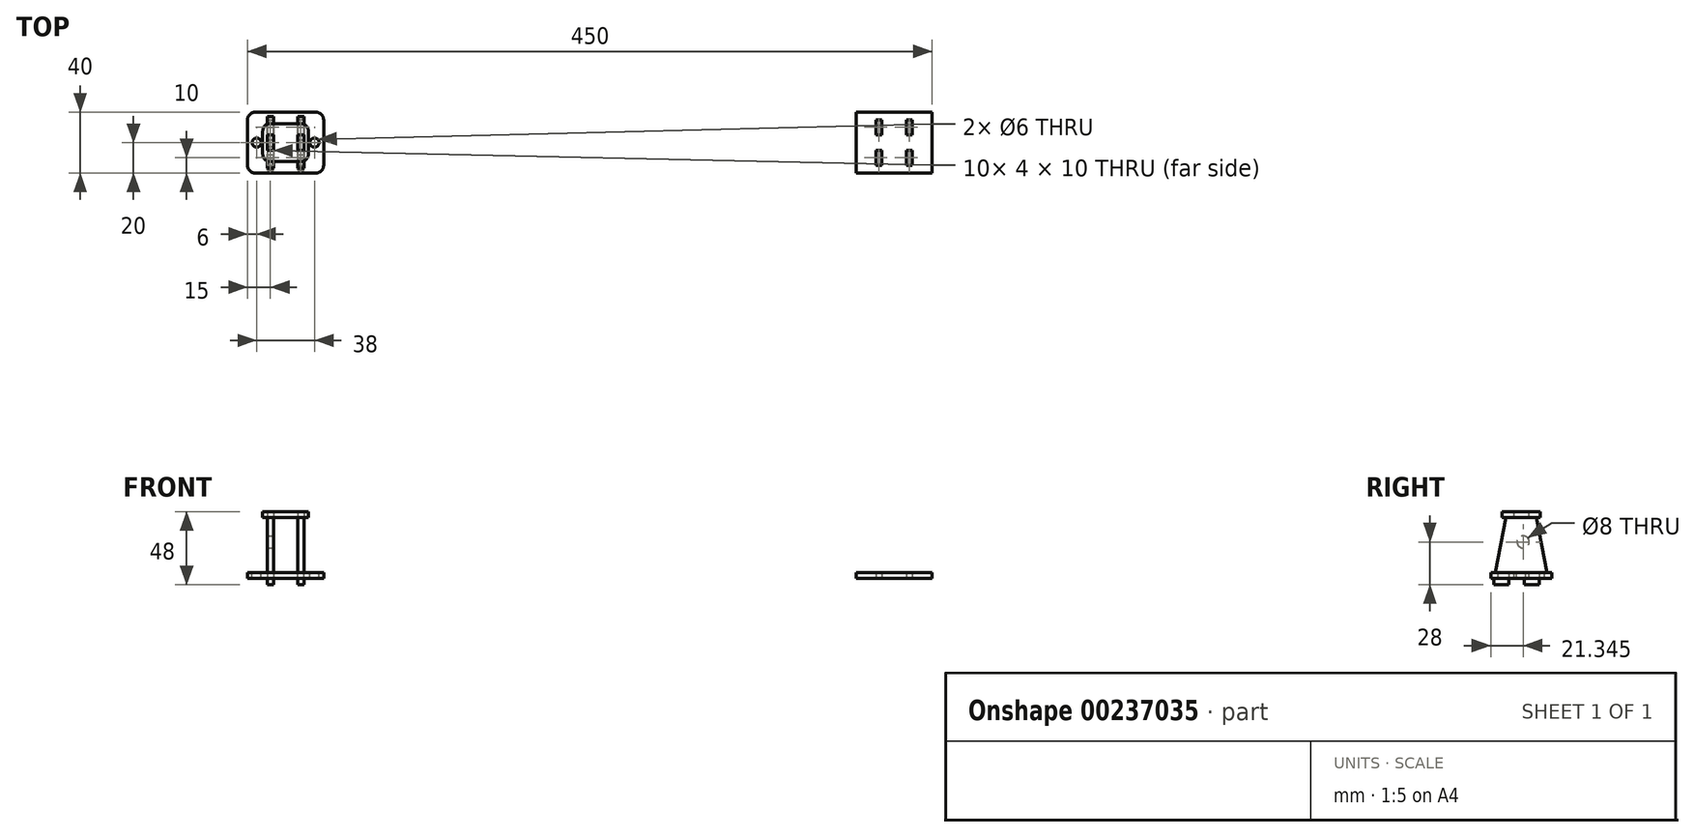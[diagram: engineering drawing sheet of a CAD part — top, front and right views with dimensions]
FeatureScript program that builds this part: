
annotation { "Feature Type Name" : "Feature", "Feature Type Description" : "" }
export const myFeature = defineFeature(function(context is Context, id is Id, definition is map)
    precondition{}
    {
        {
            var Q0;
            Q0=qCreatedBy(makeId("Top.planeOp"),FACE);
            var sketch = newSketch(context, id + "F0", { "sketchPlane" : qUnion([Q0])});
            skLineSegment(sketch, "E0.bottom", {"start": v(-200, 7.5) * mm, "end": v(200, 7.5) * mm});
            skLineSegment(sketch, "E0.top", {"start": v(-200, -7.5) * mm, "end": v(200, -7.5) * mm});
            skLineSegment(sketch, "E0.left", {"start": v(-200, 7.5) * mm, "end": v(-200, -7.5) * mm});
            skLineSegment(sketch, "E0.right", {"start": v(200, 7.5) * mm, "end": v(200, -7.5) * mm});
            skPoint(sketch, "E0.middle", {"position": v(0, 0) * mm});
            skSolve(sketch);
        }
        {
            var Q0;
            Q0=qCreatedBy(makeId("Top.planeOp"),FACE);
            var sketch = newSketch(context, id + "F1", { "sketchPlane" : qUnion([Q0])});
            skLineSegment(sketch, "E1.bottom", {"start": v(-225, 20) * mm, "end": v(-175, 20) * mm});
            skLineSegment(sketch, "E1.top", {"start": v(-225, -20) * mm, "end": v(-175, -20) * mm});
            skLineSegment(sketch, "E1.left", {"start": v(-225, 20) * mm, "end": v(-225, -20) * mm});
            skLineSegment(sketch, "E1.right", {"start": v(-175, 20) * mm, "end": v(-175, -20) * mm});
            skPoint(sketch, "E1.middle", {"position": v(-200, 0) * mm});
            skLineSegment(sketch, "E2.bottom", {"start": v(-212, 15) * mm, "end": v(-208, 15) * mm});
            skLineSegment(sketch, "E2.top", {"start": v(-212, 5) * mm, "end": v(-208, 5) * mm});
            skLineSegment(sketch, "E2.left", {"start": v(-212, 15) * mm, "end": v(-212, 5) * mm});
            skLineSegment(sketch, "E2.right", {"start": v(-208, 15) * mm, "end": v(-208, 5) * mm});
            skPoint(sketch, "E2.middle", {"position": v(-210, 10) * mm});
            skPoint(sketch, "E3.MirrorP", {"position": v(-210, -10) * mm});
            skLineSegment(sketch, "E4.MirrorCS", {"start": v(-212, -15) * mm, "end": v(-208, -15) * mm});
            skLineSegment(sketch, "E5.MirrorCS", {"start": v(-212, -15) * mm, "end": v(-212, -5) * mm});
            skLineSegment(sketch, "E6.MirrorCS", {"start": v(-208, -15) * mm, "end": v(-208, -5) * mm});
            skLineSegment(sketch, "E7.MirrorCS", {"start": v(-212, -5) * mm, "end": v(-208, -5) * mm});
            skLineSegment(sketch, "E8.MirrorCS", {"start": v(-188, -15) * mm, "end": v(-192, -15) * mm});
            skLineSegment(sketch, "E9.MirrorCS", {"start": v(-192, 15) * mm, "end": v(-192, 5) * mm});
            skLineSegment(sketch, "E10.MirrorCS", {"start": v(-188, 15) * mm, "end": v(-188, 5) * mm});
            skLineSegment(sketch, "E11.MirrorCS", {"start": v(-188, 5) * mm, "end": v(-192, 5) * mm});
            skLineSegment(sketch, "E12.MirrorCS", {"start": v(-188, 15) * mm, "end": v(-192, 15) * mm});
            skLineSegment(sketch, "E13.MirrorCS", {"start": v(-188, -15) * mm, "end": v(-188, -5) * mm});
            skLineSegment(sketch, "E14.MirrorCS", {"start": v(-188, -5) * mm, "end": v(-192, -5) * mm});
            skPoint(sketch, "E15.MirrorP", {"position": v(-190, 10) * mm});
            skPoint(sketch, "E16.MirrorP", {"position": v(-190, -10) * mm});
            skLineSegment(sketch, "E17.MirrorCS", {"start": v(-192, -15) * mm, "end": v(-192, -5) * mm});
            skLineSegment(sketch, "E18.MirrorCS", {"start": v(212, -15) * mm, "end": v(208, -15) * mm});
            skLineSegment(sketch, "E19.MirrorCS", {"start": v(188, -15) * mm, "end": v(192, -15) * mm});
            skLineSegment(sketch, "E20.MirrorCS", {"start": v(212, 15) * mm, "end": v(208, 15) * mm});
            skLineSegment(sketch, "E21.MirrorCS", {"start": v(212, -5) * mm, "end": v(208, -5) * mm});
            skLineSegment(sketch, "E22.MirrorCS", {"start": v(208, -15) * mm, "end": v(208, -5) * mm});
            skLineSegment(sketch, "E23.MirrorCS", {"start": v(212, -15) * mm, "end": v(212, -5) * mm});
            skLineSegment(sketch, "E24.MirrorCS", {"start": v(212, 5) * mm, "end": v(208, 5) * mm});
            skLineSegment(sketch, "E25.MirrorCS", {"start": v(188, 15) * mm, "end": v(192, 15) * mm});
            skLineSegment(sketch, "E26.MirrorCS", {"start": v(188, -15) * mm, "end": v(188, -5) * mm});
            skLineSegment(sketch, "E27.MirrorCS", {"start": v(192, -15) * mm, "end": v(192, -5) * mm});
            skLineSegment(sketch, "E28.MirrorCS", {"start": v(188, -5) * mm, "end": v(192, -5) * mm});
            skLineSegment(sketch, "E29.MirrorCS", {"start": v(188, 5) * mm, "end": v(192, 5) * mm});
            skLineSegment(sketch, "E30.MirrorCS", {"start": v(212, 15) * mm, "end": v(212, 5) * mm});
            skLineSegment(sketch, "E31.MirrorCS", {"start": v(188, 15) * mm, "end": v(188, 5) * mm});
            skLineSegment(sketch, "E32.MirrorCS", {"start": v(192, 15) * mm, "end": v(192, 5) * mm});
            skLineSegment(sketch, "E33.MirrorCS", {"start": v(208, 15) * mm, "end": v(208, 5) * mm});
            skLineSegment(sketch, "E34.MirrorCS", {"start": v(175, 20) * mm, "end": v(175, -20) * mm});
            skLineSegment(sketch, "E35.MirrorCS", {"start": v(225, 20) * mm, "end": v(225, -20) * mm});
            skLineSegment(sketch, "E36.MirrorCS", {"start": v(225, -20) * mm, "end": v(175, -20) * mm});
            skLineSegment(sketch, "E37.MirrorCS", {"start": v(225, 20) * mm, "end": v(175, 20) * mm});
            skPoint(sketch, "E38.MirrorP", {"position": v(210, 10) * mm});
            skPoint(sketch, "E39.MirrorP", {"position": v(190, 10) * mm});
            skPoint(sketch, "E40.MirrorP", {"position": v(200, 0) * mm});
            skPoint(sketch, "E41.MirrorP", {"position": v(190, -10) * mm});
            skPoint(sketch, "E42.MirrorP", {"position": v(210, -10) * mm});
            skSolve(sketch);
        }
        {
            var Q0;
            Q0 = qSketchRegion(id + "F1", true);
            extrude(context, id + "F2", {"entities" : qUnion([Q0]), "depth" : 4 * mm});
        }
        {
            var Q0;
            Q0=makeQuery(id+"F2.opExtrude","SWEPT_EDGE",EDGE,{"disambiguationData":[OSD([sQuery(id+"F1.wireOp",EDGE,"E1.bottom"),sQuery(id+"F1.wireOp",EDGE,"E1.right")])]});
            var Q1;
            Q1=makeQuery(id+"F2.opExtrude","SWEPT_EDGE",EDGE,{"disambiguationData":[OSD([sQuery(id+"F1.wireOp",EDGE,"E1.bottom"),sQuery(id+"F1.wireOp",EDGE,"E1.left")])]});
            var Q2;
            Q2=makeQuery(id+"F2.opExtrude","SWEPT_EDGE",EDGE,{"disambiguationData":[OSD([sQuery(id+"F1.wireOp",EDGE,"E1.top"),sQuery(id+"F1.wireOp",EDGE,"E1.right")])]});
            var Q3;
            Q3=makeQuery(id+"F2.opExtrude","SWEPT_EDGE",EDGE,{"disambiguationData":[OSD([sQuery(id+"F1.wireOp",EDGE,"E1.top"),sQuery(id+"F1.wireOp",EDGE,"E1.left")])]});
            fillet(context, id + "F3", {"entities" : qUnion([Q0, Q1, Q2, Q3]), "radius" : 5 * mm, "tangentPropagation" : true, "allowEdgeOverflow" : false});
        }
        {
            var Q0;
            Q0=makeQuery(id+"F2.opExtrude","SWEPT_FACE",FACE,{"disambiguationData":[OSD([sQuery(id+"F1.wireOp",EDGE,"E2.right")])]});
            var sketch = newSketch(context, id + "F4", { "sketchPlane" : qUnion([Q0])});
            skPoint(sketch, "E43.orphan", {"position": v(-10, 4) * mm});
            skLineSegment(sketch, "E44", {"start": v(-5, 44) * mm, "end": v(5, 44) * mm});
            skLineSegment(sketch, "E45", {"start": v(-5, 4) * mm, "end": v(-15, 4) * mm});
            skLineSegment(sketch, "E46", {"start": v(-10.11, 40) * mm, "end": v(-17, 4) * mm});
            skLineSegment(sketch, "E47", {"start": v(17, 4) * mm, "end": v(10.11, 40) * mm});
            skLineSegment(sketch, "E48", {"start": v(-12, 4) * mm, "end": v(-12, -4) * mm});
            skLineSegment(sketch, "E49", {"start": v(-12, -4) * mm, "end": v(-2, -4) * mm});
            skLineSegment(sketch, "E50", {"start": v(-2, -4) * mm, "end": v(-2, 0) * mm});
            skLineSegment(sketch, "E51", {"start": v(-2, 0) * mm, "end": v(-5, 0) * mm});
            skLineSegment(sketch, "E52", {"start": v(-5, 4) * mm, "end": v(-5, 0) * mm});
            skLineSegment(sketch, "E53", {"start": v(-12, 4) * mm, "end": v(-17, 4) * mm});
            skLineSegment(sketch, "E54", {"start": v(-5, 4) * mm, "end": v(8, 4) * mm});
            skLineSegment(sketch, "E55", {"start": v(8, 4) * mm, "end": v(8, -4) * mm});
            skLineSegment(sketch, "E56", {"start": v(8, -4) * mm, "end": v(18, -4) * mm});
            skLineSegment(sketch, "E57", {"start": v(18, -4) * mm, "end": v(18, 0) * mm});
            skLineSegment(sketch, "E58", {"start": v(18, 0) * mm, "end": v(15, 0) * mm});
            skLineSegment(sketch, "E59", {"start": v(15, 0) * mm, "end": v(15, 4) * mm});
            skLineSegment(sketch, "E60", {"start": v(15, 4) * mm, "end": v(17, 4) * mm});
            skCircle(sketch, "E61", {"center": v(-1.34, 24) * mm, "radius": 4 * mm});
            skLineSegment(sketch, "E62.top", {"start": v(-5, 40) * mm, "end": v(-10.11, 40) * mm});
            skLineSegment(sketch, "E62.left", {"start": v(-5, 44) * mm, "end": v(-5, 40) * mm});
            skLineSegment(sketch, "E63.top", {"start": v(5, 40) * mm, "end": v(10.11, 40) * mm});
            skLineSegment(sketch, "E63.left", {"start": v(5, 44) * mm, "end": v(5, 40) * mm});
            skPoint(sketch, "E64.orphan", {"position": v(-9.34, 44) * mm});
            skPoint(sketch, "E65.orphan", {"position": v(9.34, 44) * mm});
            skSolve(sketch);
        }
        {
            var Q0;
            Q0 = qSketchRegion(id + "F4", true);
            extrude(context, id + "F5", {"entities" : qUnion([Q0]), "depth" : 4 * mm});
        }
        {
            var Q0;
            Q0=makeQuery(id+"F2.opExtrude","SWEPT_FACE",FACE,{"disambiguationData":[OSD([sQuery(id+"F1.wireOp",EDGE,"E13.MirrorCS")])]});
            var sketch = newSketch(context, id + "F6", { "sketchPlane" : qUnion([Q0])});
            skLineSegment(sketch, "E66.0.0", {"start": v(-17, 4) * mm, "end": v(-12, 4) * mm});
            skLineSegment(sketch, "E66.0.1", {"start": v(-12, 4) * mm, "end": v(-12, -4) * mm});
            skLineSegment(sketch, "E66.0.2", {"start": v(-12, -4) * mm, "end": v(-2, -4) * mm});
            skLineSegment(sketch, "E66.0.3", {"start": v(-2, -4) * mm, "end": v(-2, 0) * mm});
            skLineSegment(sketch, "E66.0.4", {"start": v(-2, 0) * mm, "end": v(-5, 0) * mm});
            skLineSegment(sketch, "E66.0.5", {"start": v(-5, 0) * mm, "end": v(-5, 4) * mm});
            skLineSegment(sketch, "E66.0.6", {"start": v(-5, 4) * mm, "end": v(8, 4) * mm});
            skLineSegment(sketch, "E66.0.7", {"start": v(8, 4) * mm, "end": v(8, -4) * mm});
            skLineSegment(sketch, "E66.0.8", {"start": v(8, -4) * mm, "end": v(18, -4) * mm});
            skLineSegment(sketch, "E66.0.9", {"start": v(18, -4) * mm, "end": v(18, 0) * mm});
            skLineSegment(sketch, "E66.0.10", {"start": v(18, 0) * mm, "end": v(15, 0) * mm});
            skLineSegment(sketch, "E66.0.11", {"start": v(15, 0) * mm, "end": v(15, 4) * mm});
            skLineSegment(sketch, "E66.0.12", {"start": v(15, 4) * mm, "end": v(17, 4) * mm});
            skLineSegment(sketch, "E66.0.13", {"start": v(17, 4) * mm, "end": v(10.11, 40) * mm});
            skLineSegment(sketch, "E66.0.14", {"start": v(10.11, 40) * mm, "end": v(5, 40) * mm});
            skLineSegment(sketch, "E66.0.15", {"start": v(5, 40) * mm, "end": v(5, 44) * mm});
            skLineSegment(sketch, "E66.0.16", {"start": v(5, 44) * mm, "end": v(-5, 44) * mm});
            skLineSegment(sketch, "E66.0.17", {"start": v(-5, 44) * mm, "end": v(-5, 40) * mm});
            skLineSegment(sketch, "E66.0.18", {"start": v(-5, 40) * mm, "end": v(-10.11, 40) * mm});
            skLineSegment(sketch, "E66.0.19", {"start": v(-10.11, 40) * mm, "end": v(-17, 4) * mm});
            skSolve(sketch);
        }
        {
            var Q0;
            Q0 = qSketchRegion(id + "F6", true);
            extrude(context, id + "F7", {"entities" : qUnion([Q0]), "depth" : 4 * mm});
        }
        {
            var Q0;
            Q0=makeQuery(id+"F5.opExtrude","SWEPT_FACE",FACE,{"disambiguationData":[OSD([sQuery(id+"F4.wireOp",EDGE,"E63.top")])]});
            var sketch = newSketch(context, id + "F8", { "sketchPlane" : qUnion([Q0])});
            skLineSegment(sketch, "E67.bottom", {"start": v(-215, 12.5) * mm, "end": v(-185, 12.5) * mm});
            skLineSegment(sketch, "E67.top", {"start": v(-215, -12.5) * mm, "end": v(-185, -12.5) * mm});
            skLineSegment(sketch, "E67.left", {"start": v(-215, 12.5) * mm, "end": v(-215, -12.5) * mm});
            skLineSegment(sketch, "E67.right", {"start": v(-185, 12.5) * mm, "end": v(-185, -12.5) * mm});
            skPoint(sketch, "E67.middle", {"position": v(-200, 0) * mm});
            skLineSegment(sketch, "E68.bottom", {"start": v(-212, 5) * mm, "end": v(-208, 5) * mm});
            skLineSegment(sketch, "E68.top", {"start": v(-212, -5) * mm, "end": v(-208, -5) * mm});
            skLineSegment(sketch, "E68.left", {"start": v(-212, 5) * mm, "end": v(-212, -5) * mm});
            skLineSegment(sketch, "E68.right", {"start": v(-208, 5) * mm, "end": v(-208, -5) * mm});
            skLineSegment(sketch, "E69", {"start": v(-200, 0) * mm, "end": v(-200, 3.68) * mm, "construction": true});
            skLineSegment(sketch, "E70.MirrorCS", {"start": v(-192, 5) * mm, "end": v(-192, -5) * mm});
            skLineSegment(sketch, "E71.MirrorCS", {"start": v(-188, 5) * mm, "end": v(-192, 5) * mm});
            skLineSegment(sketch, "E72.MirrorCS", {"start": v(-188, -5) * mm, "end": v(-192, -5) * mm});
            skLineSegment(sketch, "E73.MirrorCS", {"start": v(-188, 5) * mm, "end": v(-188, -5) * mm});
            skSolve(sketch);
        }
        {
            var Q0;
            Q0 = qSketchRegion(id + "F8", true);
            extrude(context, id + "F9", {"entities" : qUnion([Q0]), "depth" : 4 * mm});
        }
        {
            var Q0;
            Q0=makeQuery(id+"F9.opExtrude","SWEPT_EDGE",EDGE,{"disambiguationData":[OSD([sQuery(id+"F8.wireOp",EDGE,"E67.top"),sQuery(id+"F8.wireOp",EDGE,"E67.left")])]});
            var Q1;
            Q1=makeQuery(id+"F9.opExtrude","SWEPT_EDGE",EDGE,{"disambiguationData":[OSD([sQuery(id+"F8.wireOp",EDGE,"E67.top"),sQuery(id+"F8.wireOp",EDGE,"E67.right")])]});
            var Q2;
            Q2=makeQuery(id+"F9.opExtrude","SWEPT_EDGE",EDGE,{"disambiguationData":[OSD([sQuery(id+"F8.wireOp",EDGE,"E67.bottom"),sQuery(id+"F8.wireOp",EDGE,"E67.right")])]});
            var Q3;
            Q3=makeQuery(id+"F9.opExtrude","SWEPT_EDGE",EDGE,{"disambiguationData":[OSD([sQuery(id+"F8.wireOp",EDGE,"E67.bottom"),sQuery(id+"F8.wireOp",EDGE,"E67.left")])]});
            fillet(context, id + "F10", {"entities" : qUnion([Q0, Q1, Q2, Q3]), "radius" : 5 * mm, "tangentPropagation" : true, "allowEdgeOverflow" : false});
        }
        {
            var Q0;
            Q0=makeQuery(id+"F2.opExtrude","CAP_FACE",FACE,{"disambiguationData":[OSD([sQuery(id+"F1.wireOp",EDGE,"E1.bottom"),sQuery(id+"F1.wireOp",EDGE,"E1.top"),sQuery(id+"F1.wireOp",EDGE,"E1.left"),sQuery(id+"F1.wireOp",EDGE,"E1.right"),sQuery(id+"F1.wireOp",EDGE,"E2.bottom"),sQuery(id+"F1.wireOp",EDGE,"E2.top"),sQuery(id+"F1.wireOp",EDGE,"E2.left"),sQuery(id+"F1.wireOp",EDGE,"E2.right"),sQuery(id+"F1.wireOp",EDGE,"E4.MirrorCS"),sQuery(id+"F1.wireOp",EDGE,"E5.MirrorCS"),sQuery(id+"F1.wireOp",EDGE,"E6.MirrorCS"),sQuery(id+"F1.wireOp",EDGE,"E7.MirrorCS"),sQuery(id+"F1.wireOp",EDGE,"E9.MirrorCS"),sQuery(id+"F1.wireOp",EDGE,"E10.MirrorCS"),sQuery(id+"F1.wireOp",EDGE,"E11.MirrorCS"),sQuery(id+"F1.wireOp",EDGE,"E12.MirrorCS"),sQuery(id+"F1.wireOp",EDGE,"E8.MirrorCS"),sQuery(id+"F1.wireOp",EDGE,"E13.MirrorCS"),sQuery(id+"F1.wireOp",EDGE,"E14.MirrorCS"),sQuery(id+"F1.wireOp",EDGE,"E17.MirrorCS")])],"isStart":false});
            var sketch = newSketch(context, id + "F11", { "sketchPlane" : qUnion([Q0])});
            skCircle(sketch, "E74", {"center": v(-219, 0) * mm, "radius": 3 * mm});
            skCircle(sketch, "E75", {"center": v(-181, 0) * mm, "radius": 3 * mm});
            skSolve(sketch);
        }
        {
            var Q0;
            Q0 = qSketchRegion(id + "F11", true);
            extrude(context, id + "F12", {"entities" : qUnion([Q0]), "operationType" : NewBodyOperationType.REMOVE, "oppositeDirection" : true, "depth" : 25 * mm});
        }
    });
